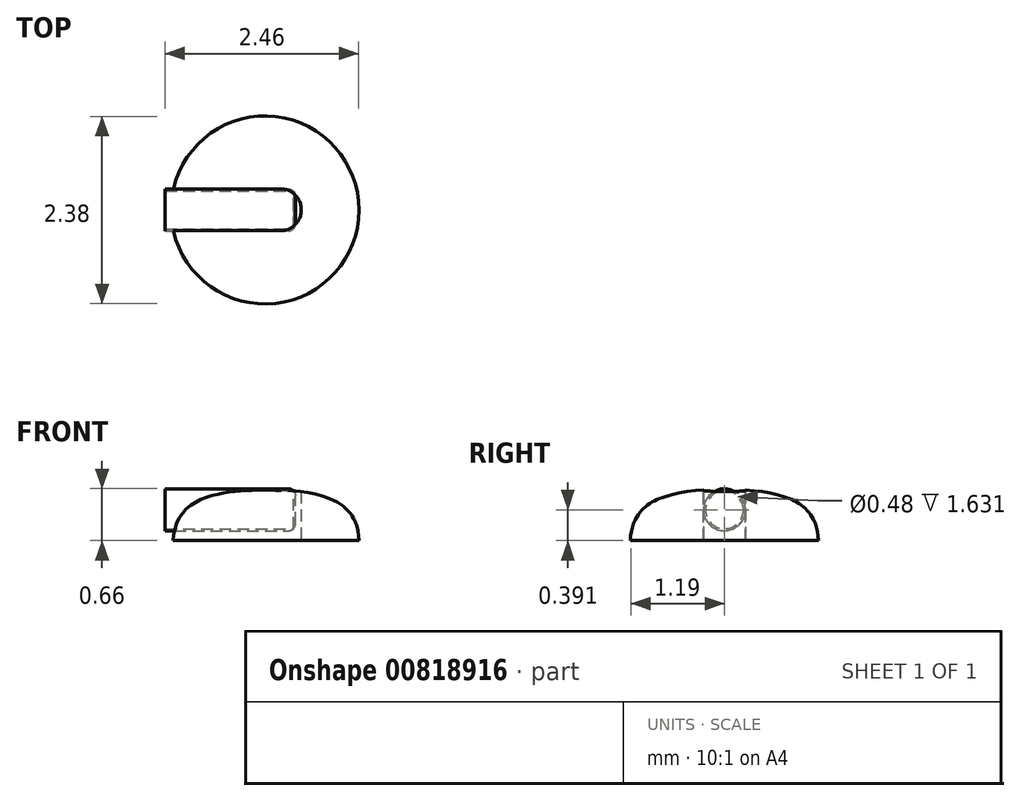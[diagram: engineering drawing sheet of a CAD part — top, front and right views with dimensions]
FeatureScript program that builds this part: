
annotation { "Feature Type Name" : "Feature", "Feature Type Description" : "" }
export const myFeature = defineFeature(function(context is Context, id is Id, definition is map)
    precondition{}
    {
        {
            var Q0;
            Q0=qCreatedBy(makeId("Front.planeOp"),FACE);
            var sketch = newSketch(context, id + "F0", { "sketchPlane" : qUnion([Q0])});
            skFitSpline(sketch, "E0", {"points": [v(0, 0.65) * mm, v(-1.2, 0) * mm], "startDerivative": vector(-1.15, -0.06) * mm, "endDerivative": vector(-0.03, -1.98) * mm});
            skLineSegment(sketch, "E1", {"start": v(-1.2, 0) * mm, "end": v(0, 0) * mm});
            skLineSegment(sketch, "E2", {"start": v(0, 0) * mm, "end": v(0, 0.65) * mm});
            skSolve(sketch);
        }
        {
            var Q0;
            Q0 = qSketchRegion(id + "F0", true);
            var Q1;
            Q1=sQuery(id+"F0.wireOp",EDGE,"E2");
            revolve(context, id + "F1", {"surfaceOperationType" : NewSurfaceOperationType.NEW, "entities" : qUnion([Q0]), "axis" : qUnion([Q1]), "revolveType" : RevolveType.FULL});
        }
        {
            var Q0;
            Q0=qCreatedBy(makeId("Top.planeOp"),FACE);
            var sketch = newSketch(context, id + "F2", { "sketchPlane" : qUnion([Q0])});
            skLineSegment(sketch, "E3.bottom", {"start": v(-1.47, 0.27) * mm, "end": v(0.46, 0.27) * mm});
            skLineSegment(sketch, "E3.top", {"start": v(-1.47, -0.26) * mm, "end": v(0.46, -0.26) * mm});
            skLineSegment(sketch, "E3.left", {"start": v(-1.47, 0.27) * mm, "end": v(-1.47, -0.26) * mm});
            skLineSegment(sketch, "E3.right", {"start": v(0.46, 0.27) * mm, "end": v(0.46, -0.26) * mm});
            skSolve(sketch);
        }
        {
            var Q0;
            Q0=makeQuery(id+"F2.imprint","IMPRINT",FACE,{"disambiguationData":[TD([[makeQuery(id+"F2.imprint","IMPRINT",EDGE,{"derivedFrom":sQuery(id+"F2.wireOp",EDGE,"E3.bottom")}),-1.0]])]});
            extrude(context, id + "F3", {"entities" : qUnion([Q0]), "operationType" : NewBodyOperationType.REMOVE, "depth" : 1.3 * mm, "offsetDistance" : 25.4 * mm});
        }
        {
            var Q0;
            Q0=makeQuery(id+"F3.boolean.opBoolean","COPY",EDGE,{"derivedFrom":makeQuery(id+"F3.opExtrude","SWEPT_EDGE",EDGE,{"disambiguationData":[OSD([sQuery(id+"F2.wireOp",EDGE,"E3.bottom"),sQuery(id+"F2.wireOp",EDGE,"E3.right")])]})});
            var Q1;
            Q1=makeQuery(id+"F3.boolean.opBoolean","COPY",EDGE,{"derivedFrom":makeQuery(id+"F3.opExtrude","SWEPT_EDGE",EDGE,{"disambiguationData":[OSD([sQuery(id+"F2.wireOp",EDGE,"E3.top"),sQuery(id+"F2.wireOp",EDGE,"E3.right")])]})});
            fillet(context, id + "F4", {"entities" : qUnion([Q0, Q1]), "radius" : 0.25 * mm, "tangentPropagation" : true, "allowEdgeOverflow" : false});
        }
        {
            var Q0;
            Q0=qCreatedBy(makeId("Right.planeOp"),FACE);
            var sketch = newSketch(context, id + "F5", { "sketchPlane" : qUnion([Q0])});
            skCircle(sketch, "E4", {"center": v(0, 0.4) * mm, "radius": 0.27 * mm});
            skSolve(sketch);
        }
        {
            var Q0;
            Q0 = qSketchRegion(id + "F5", true);
            extrude(context, id + "F6", {"entities" : qUnion([Q0]), "oppositeDirection" : true, "depth" : 1.27 * mm, "offsetDistance" : 25.4 * mm, "hasSecondDirection" : true, "secondDirectionOppositeDirection" : false, "secondDirectionDepth" : 0.39 * mm});
        }
        {
            var Q0;
            Q0=makeQuery(id+"F6.opExtrude","CAP_FACE",FACE,{"disambiguationData":[OSD([sQuery(id+"F5.wireOp",EDGE,"E4")])],"isStart":false});
            shell(context, id + "F7", {"entities" : qUnion([Q0]), "thickness" : 0.03 * mm});
        }
        {
            var Q0;
            Q0=makeQuery(id+"F6.opExtrude","CAP_EDGE",EDGE,{"disambiguationData":[OSD([sQuery(id+"F5.wireOp",EDGE,"E4")])],"isStart":true});
            fillet(context, id + "F8", {"entities" : qUnion([Q0]), "radius" : 0.09 * mm, "tangentPropagation" : true, "allowEdgeOverflow" : false});
        }
    });
